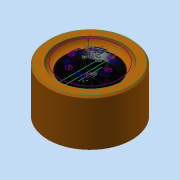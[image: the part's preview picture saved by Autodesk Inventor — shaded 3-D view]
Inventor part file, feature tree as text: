
AUTODESK INVENTOR PART (.ipt)
format: ipt  version: 2015 (Build 190159000, 159)  size: 465,920 bytes
history: native  units: in
note: dims shown in document units (in); Inventor stores cm internally (conversion verified against a paired STEP export)
features: other x3, sketch x2, projected_geometry x1
ambient origin geometry x8: Origin, YZ Plane, XZ Plane, XY Plane, X Axis, Y Axis, Z Axis, Center Point
bodies: Solid1 (feature_tree)
feature tree (6):
  other  "wheel90mm.ipt"
  sketch  "Sketch1"  dims[d0=0.3937in]
  sketch  "Sketch2"  dims[d4=0.0276in d7=0.201in d18=0.015in d19=0.03in d23=0.025in d28=2.48in d29=0.025in d30=0.025in d33=120.0deg d34=120.0deg d37=2.3622in d39=360.0deg d41=0.05in]
  other  "Solid1::wheel90mm.ipt"
  other  "TaggingFeature1"
  projected_geometry  "Projected Loop1"
